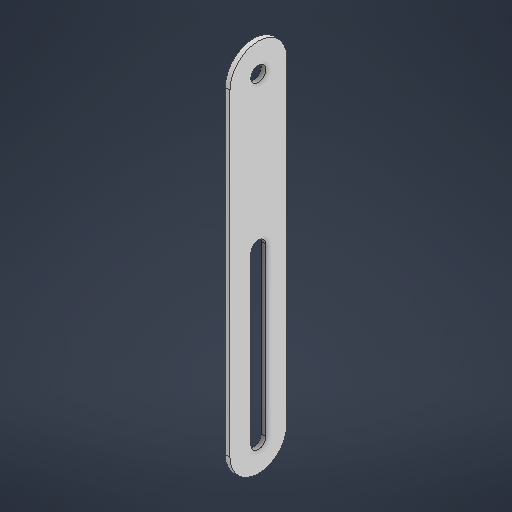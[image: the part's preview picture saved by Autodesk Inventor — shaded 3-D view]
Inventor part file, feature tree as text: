
AUTODESK INVENTOR PART (.ipt)
format: ipt  version: 2025.2 (Build 292293000, 293)  size: 197,120 bytes
history: native  units: in
note: dims shown in document units (in); Inventor stores cm internally (conversion verified against a paired STEP export)
features: extrude x1, sketch x1
ambient origin geometry x8: Origin, YZ Plane, XZ Plane, XY Plane, X Axis, Y Axis, Z Axis, Center Point
bodies: Solid1 (feature_tree)
feature tree (2):
  extrude  "Extrusion1"  Depth=0.0625in TaperAngle=0.0deg
  sketch  "Sketch1"  dims[d0=0.2in d7=0.0625in d8=0.0in d12=0.2in d13=0.1in d14=0.2in d15=0.75in]
